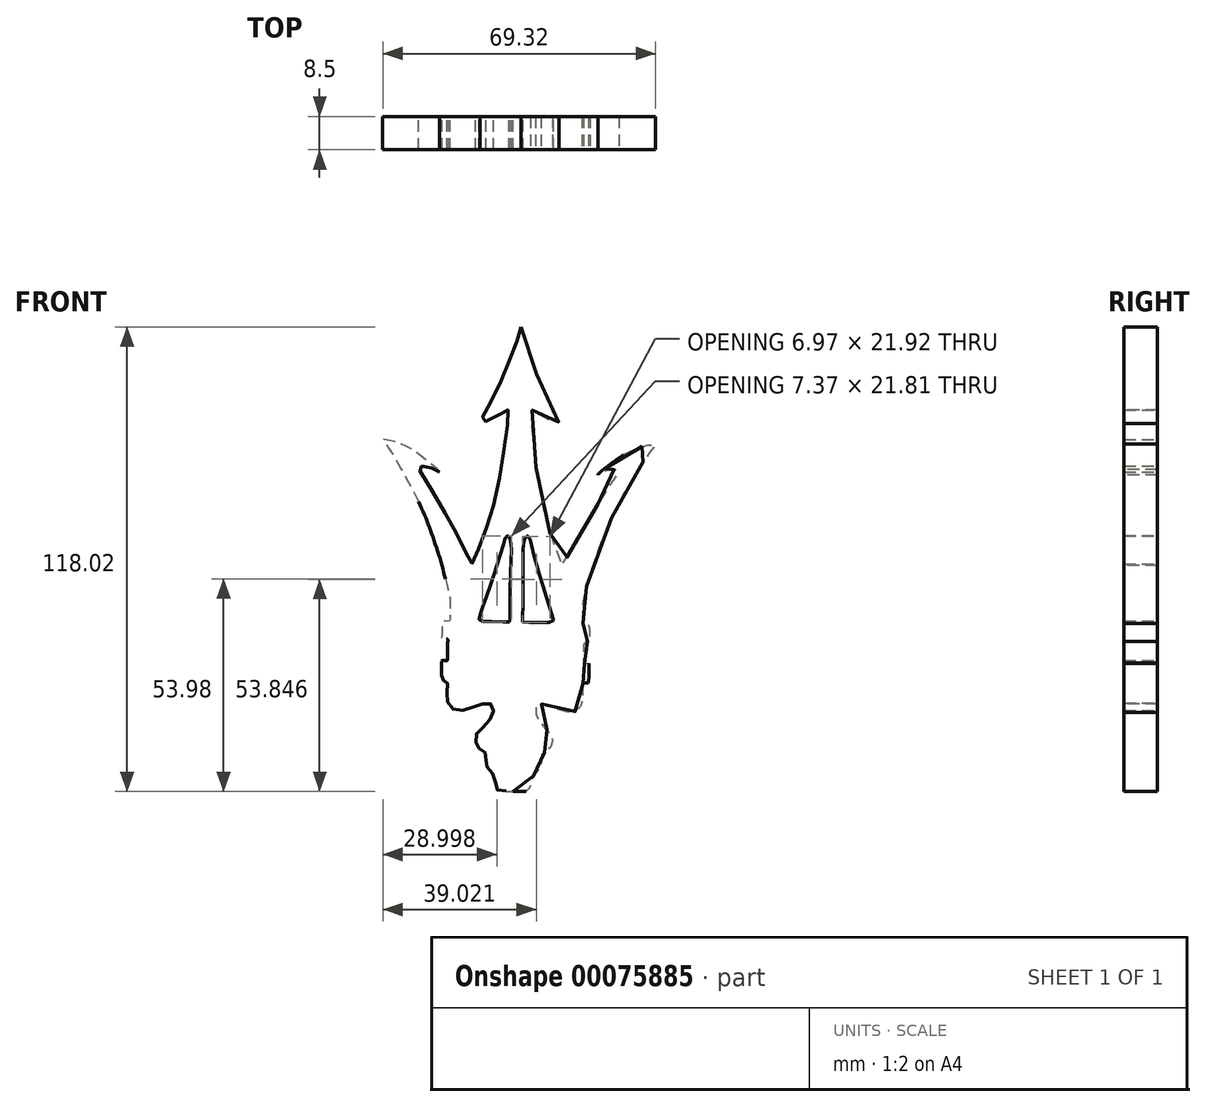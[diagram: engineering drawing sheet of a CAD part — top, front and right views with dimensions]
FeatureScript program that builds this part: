
annotation { "Feature Type Name" : "Feature", "Feature Type Description" : "" }
export const myFeature = defineFeature(function(context is Context, id is Id, definition is map)
    precondition{}
    {
        {
            var Q0;
            Q0=qCreatedBy(makeId("Front.planeOp"),FACE);
            var sketch = newSketch(context, id + "F0", { "sketchPlane" : qUnion([Q0])});
            skFitSpline(sketch, "E0", {"points": [v(0.09, 15.63) * mm, v(0.5, 14.02) * mm, v(0.94, 12.42) * mm, v(1.87, 9.6) * mm, v(3, 6.34) * mm, v(4.35, 2.6) * mm, v(6.35, -2.02) * mm, v(7.7, -4.8) * mm, v(8.57, -6.46) * mm, v(9.44, -8.33) * mm, v(9.67, -8.92) * mm, v(8.8, -8.86) * mm, v(7.72, -8.52) * mm, v(6.33, -7.76) * mm, v(4.8, -6.74) * mm, v(3.8, -5.96) * mm, v(3.37, -5.67) * mm, v(2.61, -5.61) * mm, v(2.52, -6.25) * mm, v(2.65, -8.69) * mm, v(3.24, -14.66) * mm, v(3.82, -19.77) * mm, v(4.8, -25.93) * mm, v(5.9, -31.5) * mm, v(6.96, -35.28) * mm, v(8.23, -39.18) * mm, v(9.57, -42.6) * mm, v(10.15, -44.23) * mm, v(10.57, -44.97) * mm, v(11.1, -44.46) * mm, v(11.67, -43.11) * mm, v(13.19, -40.18) * mm, v(15.16, -36.64) * mm, v(17.41, -32.93) * mm, v(20.05, -28.75) * mm, v(22.5, -24.98) * mm, v(24.72, -21.65) * mm, v(24.94, -21.28) * mm, v(24.94, -20.9) * mm, v(24.68, -20.72) * mm, v(24.13, -20.65) * mm, v(23.24, -20.65) * mm, v(22.56, -20.7) * mm, v(21.9, -20.9) * mm, v(21.06, -21.22) * mm, v(20.48, -21.52) * mm, v(19.93, -21.87) * mm, v(19.56, -21.98) * mm, v(19.82, -21.61) * mm, v(20.93, -20.65) * mm, v(22.3, -19.6) * mm, v(23.35, -18.83) * mm, v(25.3, -17.4) * mm, v(27.3, -16.23) * mm, v(29.6, -15.21) * mm, v(31.51, -14.6) * mm, v(33.54, -14.24) * mm, v(34.2, -14.22) * mm, v(34.22, -14.38) * mm, v(33.94, -14.68) * mm, v(32.9, -16.05) * mm, v(31.97, -17.36) * mm, v(30.66, -19.33) * mm, v(29.26, -21.63) * mm, v(27.43, -24.65) * mm, v(24.05, -30.7) * mm, v(21.7, -35.9) * mm, v(19.49, -41.53) * mm, v(17.41, -47.94) * mm, v(16.26, -52.04) * mm, v(15.75, -53.97) * mm, v(15.65, -55.2) * mm, v(15.65, -57) * mm, v(15.6, -58.88) * mm, v(15.6, -59.35) * mm, v(15.75, -59.71) * mm, v(16.47, -59.76) * mm, v(17.2, -59.76) * mm, v(17.48, -59.92) * mm, v(17.5, -60.72) * mm, v(17.49, -61.84) * mm, v(17.49, -63.09) * mm, v(17.49, -63.91) * mm, v(17.47, -64.24) * mm, v(17.12, -64.28) * mm, v(16.46, -64.28) * mm, v(16.07, -64.28) * mm, v(15.95, -64.36) * mm, v(15.92, -64.63) * mm, v(15.92, -65.83) * mm, v(15.92, -67.15) * mm, v(15.9, -68.12) * mm, v(15.8, -69.32) * mm, v(15.92, -69.8) * mm, v(16.36, -69.82) * mm, v(16.91, -69.8) * mm, v(17.28, -69.87) * mm, v(17.35, -70.26) * mm, v(17.28, -73.44) * mm, v(17.22, -74.25) * mm, v(17.16, -74.72) * mm, v(16.72, -74.84) * mm, v(16.11, -74.86) * mm, v(15.8, -74.95) * mm, v(15.68, -75.36) * mm, v(15.68, -76.38) * mm, v(15.68, -77.86) * mm, v(15.65, -79.3) * mm, v(15.45, -80.24) * mm, v(14.95, -81.17) * mm, v(14.23, -81.92) * mm, v(12.92, -82.33) * mm, v(11.64, -82.27) * mm, v(9.93, -81.78) * mm, v(8.33, -81.14) * mm, v(7.37, -80.76) * mm, v(5.95, -80.33) * mm, v(5.13, -80.24) * mm, v(4.35, -80.41) * mm, v(3.83, -80.94) * mm, v(3.74, -82.16) * mm, v(4, -83.2) * mm, v(4.55, -84.36) * mm, v(5.8, -86) * mm, v(6.63, -86.84) * mm, v(7.29, -87.5) * mm, v(7.92, -88.27) * mm, v(8.03, -89.29) * mm, v(7.8, -90.38) * mm, v(7.59, -91.07) * mm, v(7.26, -91.64) * mm, v(6.63, -92.03) * mm, v(6.1, -92.38) * mm, v(5.42, -92.82) * mm, v(5.2, -93.2) * mm, v(5.15, -94.18) * mm, v(5.15, -95.13) * mm, v(5.04, -95.8) * mm, v(4.78, -96.56) * mm, v(4.25, -97.16) * mm, v(3.47, -98.02) * mm, v(2.94, -98.92) * mm, v(2.47, -100.37) * mm, v(2.22, -101.32) * mm, v(2.05, -102.1) * mm, v(1.76, -102.36) * mm, v(0.84, -102.42) * mm, v(-0.78, -102.4) * mm, v(-2, -102.4) * mm], "startDerivative": vector(46.13, -244.8) * mm, "endDerivative": vector(-181.94, -0.38) * mm});
            skFitSpline(sketch, "E1", {"points": [v(0.46, -59.4) * mm, v(1.2, -59.46) * mm, v(4.8, -59.48) * mm, v(7.47, -59.5) * mm, v(8.15, -59.2) * mm, v(8.19, -58.4) * mm, v(7.7, -56.92) * mm, v(6.85, -54.35) * mm, v(5.51, -50.08) * mm, v(4.44, -46.2) * mm, v(3.59, -43.36) * mm, v(2.6, -39.43) * mm, v(2.36, -38.33) * mm, v(1.96, -37.63) * mm, v(1.64, -37.5) * mm, v(1.3, -37.7) * mm, v(0.9, -38.49) * mm, v(0.72, -39.36) * mm, v(0.6, -40.47) * mm, v(0.56, -42.87) * mm, v(0.58, -49.65) * mm, v(0.44, -56.9) * mm, v(0.36, -59.18) * mm, v(0.46, -59.4) * mm]});
            skFitSpline(sketch, "E2.MirrorCS", {"points": [v(0.1, 15.63) * mm, v(-0.37, 14.04) * mm, v(-0.86, 12.45) * mm, v(-1.89, 9.67) * mm, v(-3.14, 6.45) * mm, v(-4.62, 2.76) * mm, v(-6.78, -1.78) * mm, v(-8.23, -4.52) * mm, v(-9.16, -6.14) * mm, v(-10.1, -7.98) * mm, v(-10.34, -8.57) * mm, v(-9.47, -8.54) * mm, v(-8.38, -8.23) * mm, v(-6.96, -7.53) * mm, v(-5.39, -6.56) * mm, v(-4.37, -5.81) * mm, v(-3.93, -5.54) * mm, v(-3.17, -5.5) * mm, v(-3.1, -6.15) * mm, v(-3.32, -8.58) * mm, v(-4.12, -14.53) * mm, v(-4.88, -19.62) * mm, v(-6.08, -25.74) * mm, v(-7.38, -31.27) * mm, v(-8.56, -35.01) * mm, v(-9.98, -38.86) * mm, v(-11.43, -42.23) * mm, v(-12.07, -43.84) * mm, v(-12.52, -44.56) * mm, v(-13.04, -44.03) * mm, v(-13.55, -42.67) * mm, v(-14.96, -39.68) * mm, v(-16.81, -36.07) * mm, v(-18.93, -32.28) * mm, v(-21.42, -28.02) * mm, v(-23.73, -24.17) * mm, v(-25.83, -20.76) * mm, v(-26.04, -20.38) * mm, v(-26.02, -20) * mm, v(-25.76, -19.83) * mm, v(-25.2, -19.78) * mm, v(-24.32, -19.81) * mm, v(-23.65, -19.88) * mm, v(-22.98, -20.1) * mm, v(-22.16, -20.45) * mm, v(-21.59, -20.78) * mm, v(-21.05, -21.15) * mm, v(-20.69, -21.27) * mm, v(-20.94, -20.9) * mm, v(-22.01, -19.9) * mm, v(-23.35, -18.8) * mm, v(-24.36, -18) * mm, v(-26.27, -16.5) * mm, v(-28.2, -15.25) * mm, v(-30.48, -14.15) * mm, v(-32.37, -13.46) * mm, v(-34.38, -13.04) * mm, v(-35.04, -13) * mm, v(-35.07, -13.15) * mm, v(-34.8, -13.47) * mm, v(-33.8, -14.87) * mm, v(-32.92, -16.21) * mm, v(-31.68, -18.23) * mm, v(-30.37, -20.57) * mm, v(-28.65, -23.66) * mm, v(-25.49, -29.82) * mm, v(-23.32, -35.1) * mm, v(-21.3, -40.8) * mm, v(-19.46, -47.29) * mm, v(-18.45, -51.43) * mm, v(-18, -53.37) * mm, v(-17.95, -54.61) * mm, v(-18.01, -56.4) * mm, v(-18.03, -58.29) * mm, v(-18.04, -58.76) * mm, v(-18.21, -59.11) * mm, v(-18.94, -59.14) * mm, v(-19.66, -59.11) * mm, v(-19.95, -59.26) * mm, v(-20, -60.06) * mm, v(-20.03, -61.17) * mm, v(-20.07, -62.43) * mm, v(-20.1, -63.25) * mm, v(-20.1, -63.58) * mm, v(-19.74, -63.63) * mm, v(-19.09, -63.65) * mm, v(-18.7, -63.67) * mm, v(-18.57, -63.75) * mm, v(-18.55, -64.02) * mm, v(-18.6, -65.22) * mm, v(-18.65, -66.54) * mm, v(-18.66, -67.5) * mm, v(-18.6, -68.7) * mm, v(-18.74, -69.19) * mm, v(-19.18, -69.2) * mm, v(-19.73, -69.15) * mm, v(-20.1, -69.2) * mm, v(-20.19, -69.6) * mm, v(-20.22, -72.78) * mm, v(-20.2, -73.6) * mm, v(-20.15, -74.06) * mm, v(-19.72, -74.2) * mm, v(-19.11, -74.24) * mm, v(-18.8, -74.34) * mm, v(-18.7, -74.75) * mm, v(-18.73, -75.77) * mm, v(-18.78, -77.25) * mm, v(-18.8, -78.7) * mm, v(-18.63, -79.64) * mm, v(-18.17, -80.58) * mm, v(-17.47, -81.36) * mm, v(-16.18, -81.82) * mm, v(-14.9, -81.8) * mm, v(-13.17, -81.37) * mm, v(-11.55, -80.79) * mm, v(-10.58, -80.45) * mm, v(-9.14, -80.06) * mm, v(-8.33, -80) * mm, v(-7.55, -80.2) * mm, v(-7.05, -80.74) * mm, v(-7, -81.97) * mm, v(-7.3, -83) * mm, v(-7.9, -84.15) * mm, v(-9.2, -85.73) * mm, v(-10.06, -86.55) * mm, v(-10.74, -87.18) * mm, v(-11.4, -87.93) * mm, v(-11.54, -88.94) * mm, v(-11.36, -90.04) * mm, v(-11.16, -90.74) * mm, v(-10.86, -91.32) * mm, v(-10.24, -91.73) * mm, v(-9.73, -92.1) * mm, v(-9.06, -92.57) * mm, v(-8.86, -92.96) * mm, v(-8.84, -93.93) * mm, v(-8.87, -94.88) * mm, v(-8.78, -95.56) * mm, v(-8.55, -96.32) * mm, v(-8.05, -96.94) * mm, v(-7.29, -97.83) * mm, v(-6.8, -98.75) * mm, v(-6.38, -100.22) * mm, v(-6.16, -101.17) * mm, v(-6.02, -101.96) * mm, v(-5.74, -102.23) * mm, v(-4.82, -102.32) * mm, v(-3.2, -102.36) * mm, v(-2, -102.4) * mm], "startDerivative": vector(-54.74, -243.02) * mm, "endDerivative": vector(181.81, -6.8) * mm});
            skFitSpline(sketch, "E3.MirrorC", {"points": [v(-2.92, -59.34) * mm, v(-3.66, -59.38) * mm, v(-7.26, -59.27) * mm, v(-9.93, -59.2) * mm, v(-10.6, -58.88) * mm, v(-10.6, -58.06) * mm, v(-10.07, -56.61) * mm, v(-9.13, -54.07) * mm, v(-7.64, -49.84) * mm, v(-6.43, -46) * mm, v(-5.48, -43.2) * mm, v(-4.36, -39.3) * mm, v(-4.07, -38.21) * mm, v(-3.66, -37.53) * mm, v(-3.33, -37.4) * mm, v(-2.99, -37.63) * mm, v(-2.63, -38.42) * mm, v(-2.47, -39.3) * mm, v(-2.4, -40.42) * mm, v(-2.43, -42.82) * mm, v(-2.7, -49.59) * mm, v(-2.81, -56.84) * mm, v(-2.81, -59.12) * mm, v(-2.92, -59.34) * mm]});
            skSolve(sketch);
        }
        {
            var Q0;
            Q0=makeQuery(id+"F0.imprint","IMPRINT",FACE,{"disambiguationData":[TD([[makeQuery(id+"F0.imprint","IMPRINT",EDGE,{"derivedFrom":sQuery(id+"F0.wireOp",EDGE,"E0")}),-1.0]])]});
            extrude(context, id + "F1", {"entities" : qUnion([Q0]), "depth" : 8.5 * mm});
        }
    });
